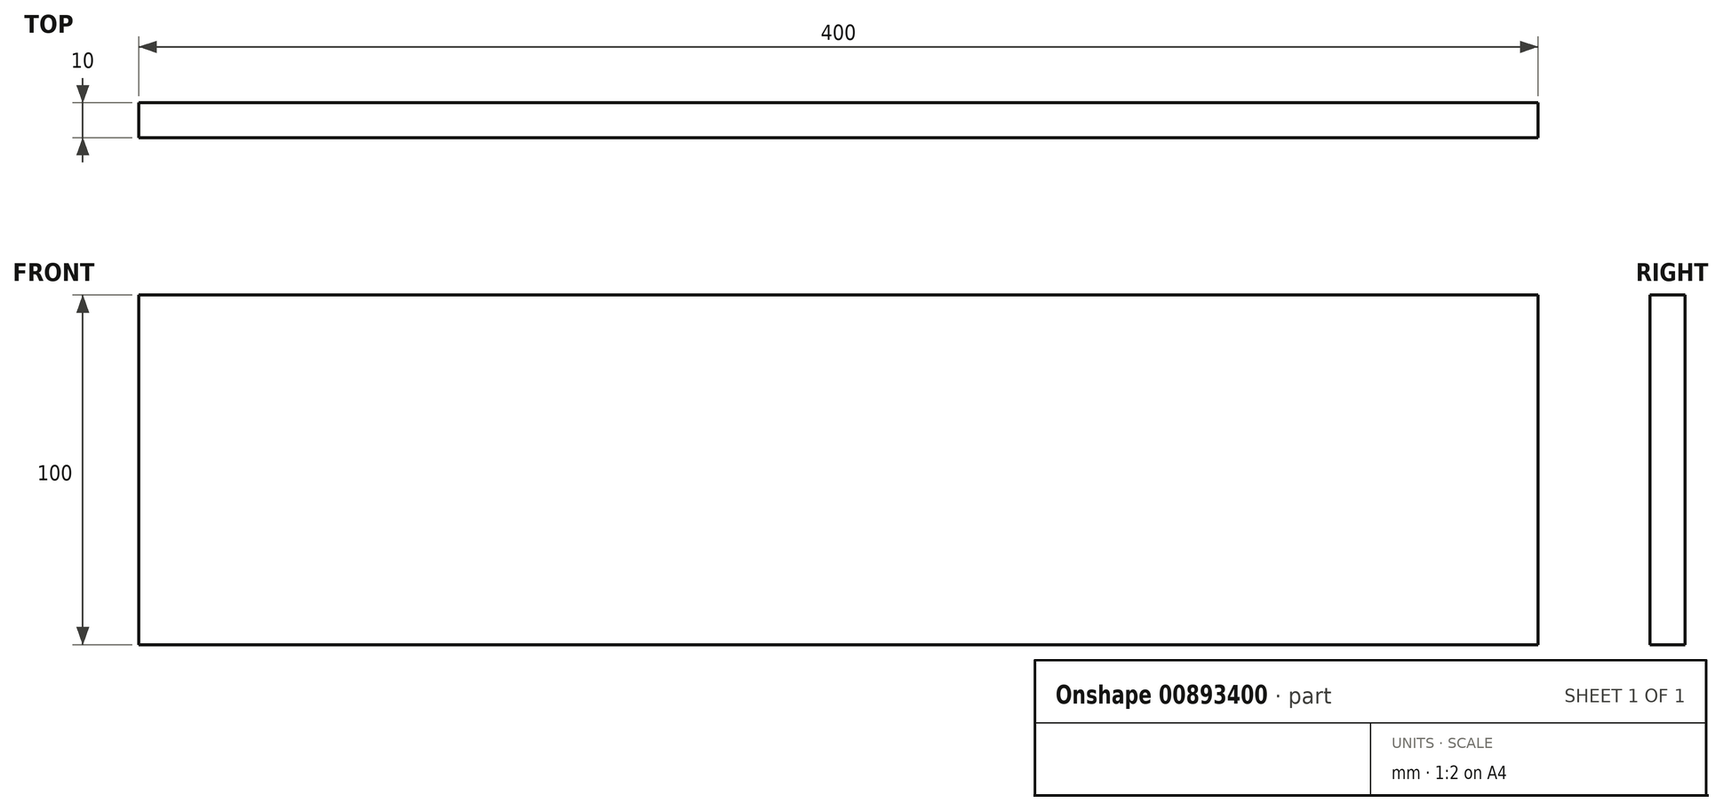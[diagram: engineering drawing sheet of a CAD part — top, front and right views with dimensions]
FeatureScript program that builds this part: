
annotation { "Feature Type Name" : "Feature", "Feature Type Description" : "" }
export const myFeature = defineFeature(function(context is Context, id is Id, definition is map)
    precondition{}
    {
        {
            var Q0;
            Q0=qCreatedBy(makeId("Front.planeOp"),FACE);
            var sketch = newSketch(context, id + "F0", { "sketchPlane" : qUnion([Q0])});
            skLineSegment(sketch, "E0.bottom", {"start": v(0, 0) * mm, "end": v(400, 0) * mm});
            skLineSegment(sketch, "E0.top", {"start": v(0, 100) * mm, "end": v(400, 100) * mm});
            skLineSegment(sketch, "E0.left", {"start": v(0, 0) * mm, "end": v(0, 100) * mm});
            skLineSegment(sketch, "E0.right", {"start": v(400, 0) * mm, "end": v(400, 100) * mm});
            skSolve(sketch);
        }
        {
            var Q0;
            Q0 = qSketchRegion(id + "F0", true);
            extrude(context, id + "F1", {"entities" : qUnion([Q0]), "depth" : 10 * mm, "offsetDistance" : 25 * mm});
        }
    });
